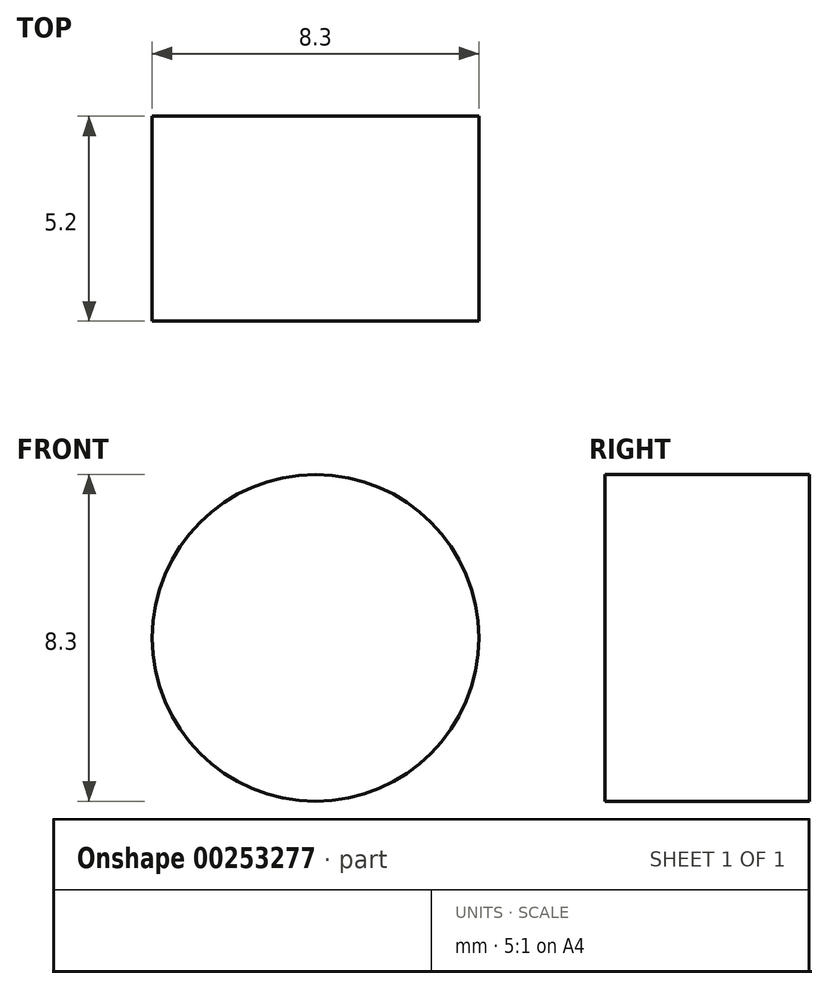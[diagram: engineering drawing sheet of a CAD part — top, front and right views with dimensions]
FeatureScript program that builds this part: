
annotation { "Feature Type Name" : "Feature", "Feature Type Description" : "" }
export const myFeature = defineFeature(function(context is Context, id is Id, definition is map)
    precondition{}
    {
        {
            var Q0;
            Q0=qCreatedBy(makeId("Front.planeOp"),FACE);
            var sketch = newSketch(context, id + "F0", { "sketchPlane" : qUnion([Q0])});
            skCircle(sketch, "E0", {"center": v(0, 0) * mm, "radius": 4.15 * mm});
            skSolve(sketch);
        }
        {
            var Q0;
            Q0=makeQuery(id+"F0.imprint","IMPRINT",FACE,{"disambiguationData":[TD([[makeQuery(id+"F0.imprint","IMPRINT",EDGE,{"derivedFrom":sQuery(id+"F0.wireOp",EDGE,"E0")}),1.0]])]});
            extrude(context, id + "F1", {"entities" : qUnion([Q0]), "depth" : 5.2 * mm});
        }
    });
